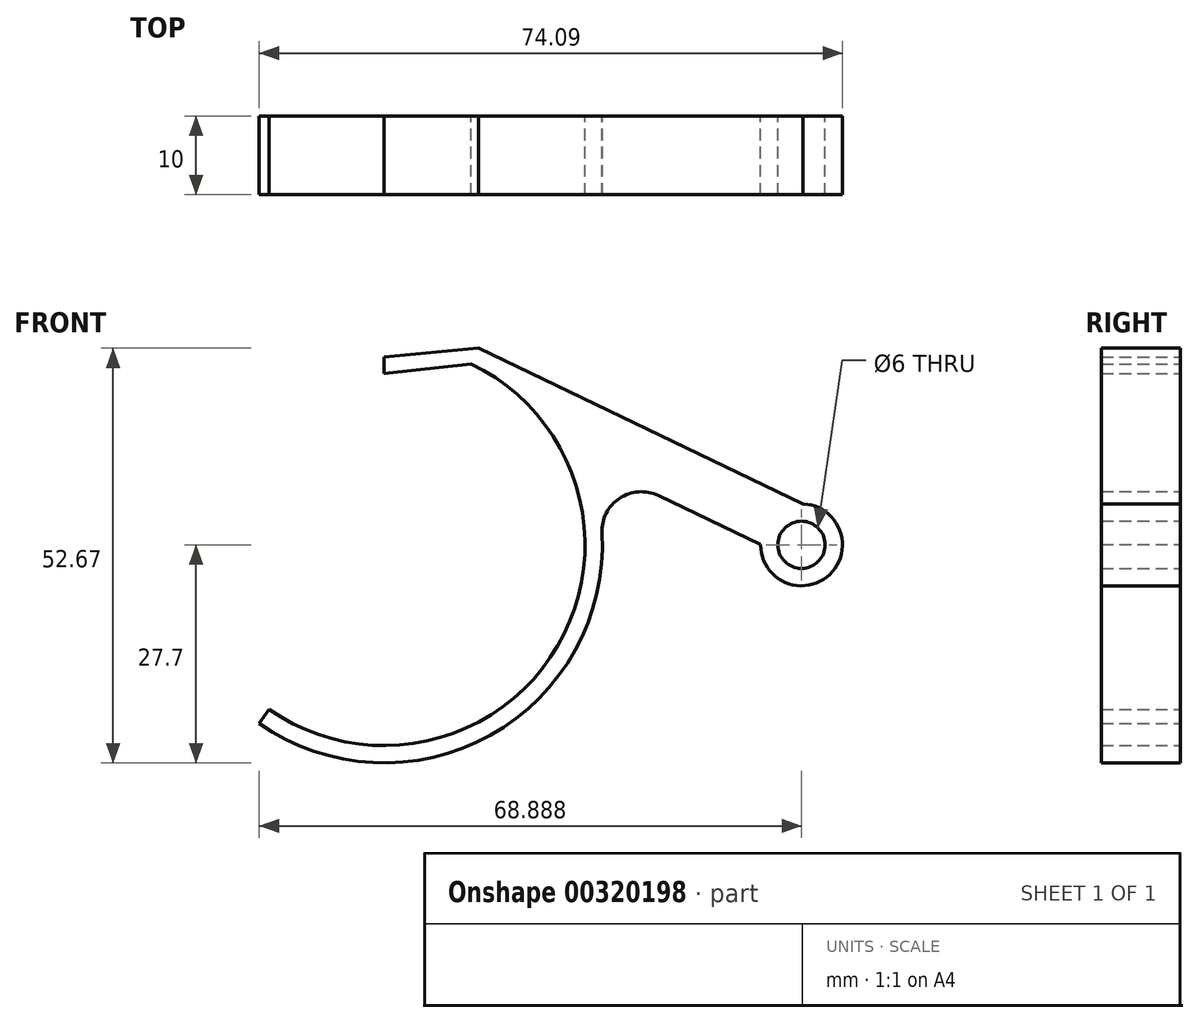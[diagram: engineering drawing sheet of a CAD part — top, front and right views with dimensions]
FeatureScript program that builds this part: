
annotation { "Feature Type Name" : "Feature", "Feature Type Description" : "" }
export const myFeature = defineFeature(function(context is Context, id is Id, definition is map)
    precondition{}
    {
        {
            var Q0;
            Q0=qCreatedBy(makeId("Front.planeOp"),FACE);
            var sketch = newSketch(context, id + "F0", { "sketchPlane" : qUnion([Q0])});
            skArc(sketch, "E0", {"start": v(-37.29, -20.89) * mm, "mid": v(-0.65, -12.87) * mm, "end": v(-11.63, 23) * mm});
            skCircle(sketch, "E1", {"center": v(30.34, 0) * mm, "radius": 3 * mm});
            skArc(sketch, "E2.0", {"start": v(-38.55, -22.7) * mm, "mid": v(-9.22, -24.22) * mm, "end": v(5, 1.48) * mm});
            skArc(sketch, "E3.0", {"start": v(25.14, 0.03) * mm, "mid": v(33.93, -3.76) * mm, "end": v(30.55, 5.2) * mm});
            skLineSegment(sketch, "E4", {"start": v(-22.66, 0) * mm, "end": v(-22.66, 23.83) * mm, "construction": true});
            skLineSegment(sketch, "E5", {"start": v(-22.66, 0) * mm, "end": v(-48.32, -36.64) * mm, "construction": true});
            skLineSegment(sketch, "E6", {"start": v(-22.66, 0) * mm, "end": v(-10.68, 24.97) * mm, "construction": true});
            skPoint(sketch, "E7.endSnap0", {"position": v(-22.66, 24.79) * mm});
            skLineSegment(sketch, "E8", {"start": v(-38.55, -22.7) * mm, "end": v(-37.29, -20.89) * mm});
            skLineSegment(sketch, "E9", {"start": v(-11.63, 23) * mm, "end": v(-22.66, 21.78) * mm});
            skLineSegment(sketch, "E10", {"start": v(-22.66, 21.78) * mm, "end": v(-22.66, 23.83) * mm});
            skLineSegment(sketch, "E11", {"start": v(-22.66, 23.83) * mm, "end": v(-10.68, 24.97) * mm});
            skPoint(sketch, "E12.trimOffspring.end.orphan", {"position": v(-22.66, 49.57) * mm});
            skPoint(sketch, "E13.orphan", {"position": v(-2.42, 23.72) * mm});
            skLineSegment(sketch, "E14", {"start": v(-10.68, 24.97) * mm, "end": v(30.55, 5.2) * mm});
            skLineSegment(sketch, "E15.0", {"start": v(12.15, 6.26) * mm, "end": v(25.2, 0) * mm});
            skArc(sketch, "E16.filletArc", {"start": v(12.15, 6.26) * mm, "mid": v(7.22, 5.9) * mm, "end": v(5, 1.48) * mm});
            skSolve(sketch);
        }
        {
            var Q0;
            Q0=makeQuery(id+"F0.imprint","IMPRINT",FACE,{"disambiguationData":[TD([[makeQuery(id+"F0.imprint","IMPRINT",EDGE,{"derivedFrom":sQuery(id+"F0.wireOp",EDGE,"E0")}),-1.0]])]});
            extrude(context, id + "F1", {"entities" : qUnion([Q0]), "depth" : 10 * mm});
        }
    });
